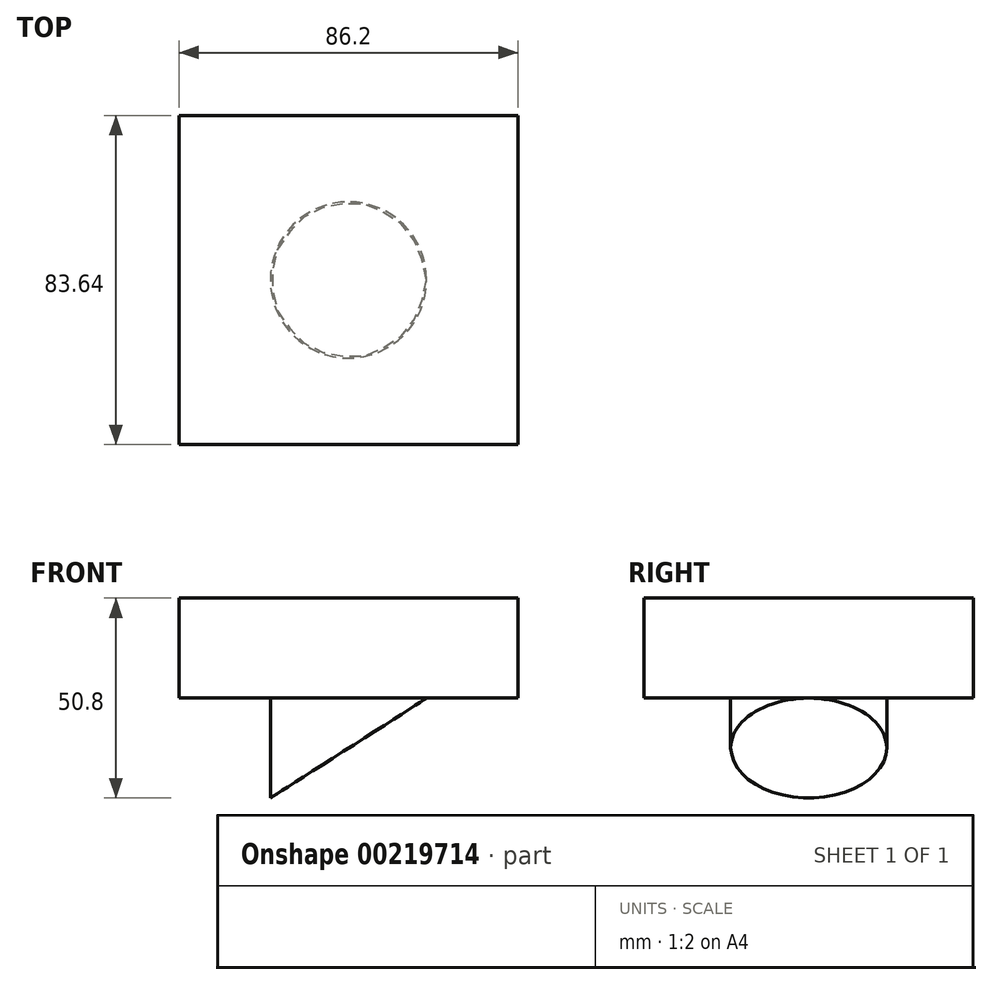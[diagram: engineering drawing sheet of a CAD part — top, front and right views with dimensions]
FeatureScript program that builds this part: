
annotation { "Feature Type Name" : "Feature", "Feature Type Description" : "" }
export const myFeature = defineFeature(function(context is Context, id is Id, definition is map)
    precondition{}
    {
        {
            var Q0;
            Q0=qCreatedBy(makeId("Top.planeOp"),FACE);
            var sketch = newSketch(context, id + "F0", { "sketchPlane" : qUnion([Q0])});
            skLineSegment(sketch, "E0.bottom", {"start": v(43.1, -41.82) * mm, "end": v(-43.1, -41.82) * mm});
            skLineSegment(sketch, "E0.top", {"start": v(43.1, 41.82) * mm, "end": v(-43.1, 41.82) * mm});
            skLineSegment(sketch, "E0.left", {"start": v(43.1, -41.82) * mm, "end": v(43.1, 41.82) * mm});
            skLineSegment(sketch, "E0.right", {"start": v(-43.1, -41.82) * mm, "end": v(-43.1, 41.82) * mm});
            skPoint(sketch, "E0.middle", {"position": v(0, 0) * mm});
            skSolve(sketch);
        }
        {
            var Q0;
            Q0 = qSketchRegion(id + "F0", true);
            extrude(context, id + "F1", {"entities" : qUnion([Q0]), "depth" : 25.4 * mm});
        }
        {
            var Q0;
            Q0=qCreatedBy(makeId("Top.planeOp"),FACE);
            var sketch = newSketch(context, id + "F2", { "sketchPlane" : qUnion([Q0])});
            skCircle(sketch, "E1", {"center": v(0, 0) * mm, "radius": 19.85 * mm});
            skSolve(sketch);
        }
        {
            var Q0;
            Q0=makeQuery(id+"F2.imprint","IMPRINT",FACE,{"disambiguationData":[TD([[makeQuery(id+"F2.imprint","IMPRINT",EDGE,{"derivedFrom":sQuery(id+"F2.wireOp",EDGE,"E1")}),1.0]])]});
            var Q1;
            Q1=sQuery(id+"F2.wireOp",EDGE,"E1");
            extrude(context, id + "F3", {"entities" : qUnion([Q0]), "operationType" : NewBodyOperationType.ADD, "surfaceEntities" : qUnion([Q1]), "oppositeDirection" : true, "depth" : 25.4 * mm});
        }
        {
            var Q0;
            Q0=makeQuery(id+"F1.opExtrude","SWEPT_FACE",FACE,{"disambiguationData":[OSD([sQuery(id+"F0.wireOp",EDGE,"E0.top")])]});
            var sketch = newSketch(context, id + "F4", { "sketchPlane" : qUnion([Q0])});
            skLineSegment(sketch, "E2.0", {"start": v(-19.85, -25.4) * mm, "end": v(19.85, -25.4) * mm});
            skLineSegment(sketch, "E3", {"start": v(-19.85, -25.4) * mm, "end": v(-19.85, 0) * mm});
            skLineSegment(sketch, "E4", {"start": v(19.85, -25.4) * mm, "end": v(-19.85, 0) * mm});
            skSolve(sketch);
        }
        {
            var Q0;
            Q0 = qSketchRegion(id + "F4", true);
            extrude(context, id + "F5", {"entities" : qUnion([Q0]), "operationType" : NewBodyOperationType.REMOVE, "endBound" : BoundingType.THROUGH_ALL, "oppositeDirection" : true, "depth" : 25.4 * mm});
        }
    });
